# Revit family: 0047887_Feilo Sylvania Lighting Fixture_SYLPROOF_LED_44W_1265MM_T_4000K_E3
name_source: partatom
category: Lighting Fixtures
revit_build: Autodesk Revit 2015 (Build: 20140606_1530(x64)
units: mm (PartAtom-declared; Revit-internal decimal feet)

## types (1)
- 0047887
    Apparent Load = 44 VA
    Assembly Code = D5020200
    Body Material = Polycarbonate_Body_Sylvania_Brite White
    Bracket-Diffuser Material = <By Category>
    Bracket-Mounting Material = <By Category>
    CRI ( Ra ) = 85
    Catalog Number = 0047887
    Color Filter = 16777215
    Default Elevation = 0 mm  [stored 0 ft]
    Description = Weather resistant LED Luminaire
    Diffuser Brackets Length = 1105 mm
    Diffuser Material = Polycarbonate_Diffuser_Sylvania_Clear
    Dimming Lamp Color Temperature Shift = <None>
    Emit Shape Visible in Rendering = No
    Emit from Rectangle Length = 1245 mm  [stored 4.08465 ft]
    Emit from Rectangle Width = 95 mm  [stored 0.31168 ft]
    Height = 91 mm  [stored 0.298556 ft]
    Housing ( Degree ) = 850 C
    IP rating = 65
    LOR Light Output Ratio ( % ) = 100 %
    Lamp = 43.6W LED
    Lamp - Single = No
    Lamp - Twin = Yes
    Lamp Comments = Integrated LED
    Lamp Material = Acrylic High Luminance Glass_Lamp_Sylvania_White
    Length = 1265 mm  [stored 4.15026 ft]
    Length Help = 1205 mm
    Manufacturer = Feilo Sylvania
    Model = START WATERPROOF LED 1265MM TWIN 4000K E3
    Mounting Brackets Length = 390 mm  [stored 1.27953 ft]
    Mounting Brackets Width = 54 mm  [stored 0.177165 ft]
    Number of Diffuser Brackets = 3
    Photometric Web File = 0047887_SYLPROOFLED44W1265MMT4000KE3-201524.ies
    Product Family = Start Waterproof LED
    Side Void Width = 70 mm  [stored 0.229659 ft]
    Tilt Angle = -90.00°
    Voltage = 240 V
    Voltage Comments = UNV (Universal Voltage; 220-240 Volt)
    Weight = 2.59kg
    Width = 123 mm  [stored 0.403543 ft]
    Width Help = 55 mm  [stored 0.180446 ft]

note: [stored X ft] marks values corroborated as IEEE doubles in the binary element streams (Revit-internal decimal feet)

## geometry (parser evidence)
native form markers: Blend x5, Sweep x15
no freeform markers — native parametric forms only
